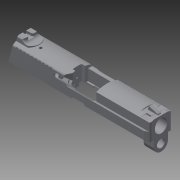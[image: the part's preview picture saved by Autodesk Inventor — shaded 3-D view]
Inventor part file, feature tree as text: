
AUTODESK INVENTOR PART (.ipt)
format: ipt  version: 2014 SP1 (Build 180222100, 222)  size: 2,646,528 bytes
history: native  units: in
note: dims shown in document units (in); Inventor stores cm internally (conversion verified against a paired STEP export)
features: sketch x85, projected_geometry x80, extrude x69, plane x11, other x6, fillet x5, mirror x5, loft x4, revolve x4, chamfer x2, emboss x2, pattern_linear x1, reference x1
ambient origin geometry x8: Origin, YZ Plane, XZ Plane, XY Plane, X Axis, Y Axis, Z Axis, Center Point
bodies: Body1 (feature_tree), Body2 (feature_tree), Body3 (feature_tree)
feature tree (275):
  other  "Slide"
  extrude  "Extrusion1"  Depth=0.868in
  sketch  "Sketch3"  dims[d5=1.0545in d6=0.0in d7=105.0deg]
  loft  "Loft1"
  extrude  "Extrusion2"  TaperAngle=105.0deg  [1 undecoded]
  extrude  "Extrusion3"  Depth=0.5in
  extrude  "Extrusion4"  Depth=0.5in
  other  "Top Plane"
  extrude  "Extrusion5"  TaperAngle=0.0deg  [1 undecoded]
  extrude  "Extrusion6"  Depth=0.6385in
  extrude  "Extrusion7"  Depth=0.3515in
  extrude  "Extrusion8"  Depth=0.595in TaperAngle=0.0deg
  extrude  "Extrusion9"  Depth=2.4555in
  plane  "Work Plane2"
  extrude  "Extrusion10"  Depth=0.595in TaperAngle=0.0deg
  extrude  "Extrusion11"  Depth=0.595in TaperAngle=0.0deg
  revolve  "Revolution1"  [1 undecoded]
  extrude  "Extrusion12"  Depth=0.507in
  extrude  "Extrusion13"  Depth=0.125in
  extrude  "Extrusion14"  Depth=0.588in
  extrude  "Extrusion15"  Depth=0.1138in
  sketch  "Sketch22"  dims[d52=0.091in d53=0.182in]
  plane  "Work Plane5"
  extrude  "Extrusion16"  Depth=0.135in
  extrude  "Extrusion17"  Depth=0.8675in
  extrude  "Extrusion18"  Depth=0.182in
  extrude  "Extrusion19"  Depth=0.553in
  extrude  "Extrusion20"  Depth=0.581in TaperAngle=0.0deg
  extrude  "Extrusion21"  Depth=0.058in
  sketch  "Sketch30"  dims[d75=0.6285in d76=0.0in d77=30.0deg]
  other  "Work Point1"
  sketch  "Sketch31"  dims[d78=0.6285in d79=0.0in d80=1.2325in]
  sketch  "Sketch33"  dims[d83=0.6285in d84=0.0in d85=0.0902in]
  sketch  "Sketch32"  dims[d81=0.36in d82=0.07in]
  loft  "Loft3"
  revolve  "Revolution2"  [1 undecoded]
  extrude  "Extrusion22"  Depth=0.588in
  extrude  "Extrusion23"  TaperAngle=30.0deg  [1 undecoded]
  extrude  "Extrusion24"  Depth=1.2325in
  sketch  "Sketch38"  dims[d98=0.236in d99=0.0555in d100=0.0in]
  extrude  "Extrusion25"  Depth=0.07in
  extrude  "Extrusion26"  Depth=0.0902in
  extrude  "Extrusion27"  Depth=1.906in
  extrude  "Extrusion28"  Depth=0.2325in TaperAngle=0.0deg
  extrude  "Extrusion29"  Depth=0.6285in TaperAngle=0.0deg
  extrude  "Extrusion30"  Depth=0.1195in
  extrude  "Extrusion31"  Depth=0.0555in TaperAngle=0.0deg
  extrude  "Extrusion32"  Depth=0.063in TaperAngle=0.0deg
  extrude  "Extrusion33"  Depth=0.05in
  plane  "Work Plane6"
  extrude  "Extrusion34"  Depth=0.2in
  extrude  "Extrusion35"  Depth=0.125in
  extrude  "Extrusion36"  TaperAngle=0.0deg  [1 undecoded]
  extrude  "Extrusion37"  TaperAngle=45.0deg  [1 undecoded]
  plane  "Work Plane7"
  extrude  "Extrusion38"  Depth=0.2in
  extrude  "Extrusion39"  Depth=0.6315in
  extrude  "Extrusion40"  Depth=0.4688in
  extrude  "Extrusion41"  Depth=0.942in
  fillet  "Fillet1"  Radius=0.126in
  plane  "Work Plane8"
  extrude  "Extrusion42"  Depth=0.205in
  extrude  "Extrusion43"  Depth=0.1585in
  pattern_linear  "Rectangular Pattern1"  Spacing1=0.1345in  [1 undecoded]
  mirror  "Mirror1"
  extrude  "Extrusion44"  Depth=0.015in
  extrude  "Extrusion55"  Depth=0.015in
  sketch  "Sketch69"  dims[d162=0.167in]
  chamfer  "Chamfer2"  Distance=0.4735in
  other  "Work Point2"
  extrude  "Extrusion56"  Depth=0.015in
  loft  "Loft5"
  extrude  "Extrusion45"  Depth=0.015in
  mirror  "Mirror2"
  extrude  "Extrusion46"  [1 undecoded]
  extrude  "Extrusion47"  Depth=0.015in
  extrude  "Extrusion48"  Depth=0.015in
  extrude  "Extrusion49"  Depth=0.015in
  sketch  "Sketch62"  dims[d152=0.133in]
  extrude  "Extrusion50"  Depth=0.015in
  extrude  "Extrusion51"  Depth=0.015in
  extrude  "Extrusion52"  Depth=0.015in TaperAngle=0.0deg
  extrude  "Extrusion53"  Depth=0.015in
  fillet  "Fillet2"  Radius=0.118in
  fillet  "Fillet3"  Radius=0.016in
  chamfer  "Chamfer1"  Distance=3.937in
  sketch  "Sketch67"  dims[d159=0.13in]
  emboss  "Emboss1"
  emboss  "Emboss2"
  extrude  "Extrusion54"  TaperAngle=60.0deg  [1 undecoded]
  extrude  "Extrusion57"  Depth=0.015in
  mirror  "Mirror3"
  fillet  "Fillet4"  Radius=0.059in
  extrude  "Extrusion58"  Depth=0.015in
  extrude  "Extrusion59"  Depth=0.015in TaperAngle=0.0deg
  revolve  "Revolution3"  [1 undecoded]
  extrude  "Extrusion60"  Depth=0.015in
  extrude  "Extrusion61"  Depth=0.015in TaperAngle=0.0deg
  plane  "Work Plane9"
  extrude  "Extrusion62"  Depth=0.015in
  sketch  "Sketch81"  dims[d177=0.12in]
  plane  "Work Plane10"
  sketch  "Sketch83"  dims[d178=0.289in]
  loft  "Loft6"
  extrude  "Extrusion64"  Depth=0.015in TaperAngle=0.0deg
  extrude  "Extrusion65"  Depth=0.015in
  extrude  "Extrusion66"  Depth=0.015in TaperAngle=0.0deg
  extrude  "Extrusion67"  Depth=0.015in
  extrude  "Extrusion68"  Depth=0.015in TaperAngle=0.0deg
  extrude  "Extrusion69"  Depth=0.015in TaperAngle=0.0deg
  plane  "Work Plane11"
  revolve  "Revolution4"  [1 undecoded]
  mirror  "Mirror4"
  extrude  "Extrusion70"  Depth=0.015in TaperAngle=0.0deg
  fillet  "Fillet5"  Radius=0.374in
  mirror  "Mirror5"
  plane  "Work Plane12"
  sketch  "Sketch1"  dims[d0=6.506in d1=0.868in]
  sketch  "Sketch2"  dims[d2=1.0545in d3=0.0in d4=1.25in]
  projected_geometry  "Projected Loop1"
  sketch  "Sketch4"  dims[d8=1.625in d9=0.5in]
  projected_geometry  "Projected Loop2"
  sketch  "Sketch5"  dims[d10=1.625in d11=0.5in]
  projected_geometry  "Projected Loop3"
  sketch  "Sketch6"  dims[d12=0.0in d13=90.0deg d14=0.0in d15=90.0deg]
  projected_geometry  "Projected Loop4"
  sketch  "Sketch7"  dims[d16=0.471in d17=0.6385in]
  projected_geometry  "Projected Loop5"
  sketch  "Sketch8"  dims[d18=0.595in d19=0.0in d20=0.3515in]
  projected_geometry  "Projected Loop6"
  sketch  "Sketch9"  dims[d21=0.1435in d22=0.595in d23=0.0in]
  sketch  "Sketch10"  dims[d24=0.666in d25=2.4555in]
  projected_geometry  "Projected Loop7"
  sketch  "Sketch11"  dims[d26=1.2025in d27=0.595in d28=0.0in]
  projected_geometry  "Projected Loop8"
  sketch  "Sketch12"  dims[d29=0.69in d30=0.595in d31=0.0in]
  projected_geometry  "Projected Loop9"
  sketch  "Sketch13"  dims[d32=0.154in d33=0.41in]
  projected_geometry  "Projected Loop10"
  sketch  "Sketch14"  dims[d34=0.595in d35=0.0in d36=0.507in]
  projected_geometry  "Projected Loop11"
  sketch  "Sketch17"  dims[d37=0.787in d40=0.125in]
  sketch  "Sketch18"  dims[d41=0.588in d42=0.588in]
  projected_geometry  "Projected Loop13"
  sketch  "Sketch19"  dims[d43=0.724in d44=0.0in d45=0.1138in]
  projected_geometry  "Projected Loop14"
  sketch  "Sketch20"  dims[d47=0.135in d48=0.135in]
  sketch  "Sketch21"  dims[d49=0.2685in d50=0.0in d51=0.8675in]
  plane  "Work Plane3"
  plane  "Work Plane4"
  sketch  "Sketch24"  dims[d54=0.2685in d55=0.0in d56=0.553in]
  sketch  "Sketch25"  dims[d57=0.223in d58=0.581in d59=0.0in]
  projected_geometry  "Projected Loop15"
  sketch  "Sketch26"  dims[d66=0.268in d67=0.058in]
  projected_geometry  "Projected Loop16"
  projected_geometry  "Projected Loop17"
  sketch  "Sketch27"  dims[d68=90.0deg d69=0.057in]
  projected_geometry  "Projected Loop18"
  sketch  "Sketch28"  dims[d70=0.057in d71=0.0625in]
  projected_geometry  "Projected Loop19"
  sketch  "Sketch29"  dims[d72=0.031in d73=0.0in d74=0.588in]
  projected_geometry  "Projected Loop20"
  projected_geometry  "Projected Loop21"
  sketch  "Sketch34"  dims[d86=0.4435in d87=1.906in]
  projected_geometry  "Projected Loop22"
  sketch  "Sketch35"  dims[d88=0.2405in d89=0.0in d90=0.2325in]
  projected_geometry  "Projected Loop23"
  sketch  "Sketch36"  dims[d92=0.18in d93=0.6285in d94=0.0in]
  sketch  "Sketch37"  dims[d95=0.6285in d96=0.0in d97=0.1195in]
  projected_geometry  "Projected Loop24"
  sketch  "Sketch39"  dims[d101=0.0555in d102=0.0in d103=0.063in d104=0.0in]
  projected_geometry  "Projected Loop25"
  sketch  "Sketch40"  dims[d105=0.126in d106=0.0in d107=0.05in]
  projected_geometry  "Projected Loop26"
  sketch  "Sketch41"  dims[d108=0.125in d109=0.2in]
  projected_geometry  "Projected Loop27"
  sketch  "Sketch42"  dims[d110=45.0deg d111=0.125in]
  sketch  "Sketch43"  dims[d112=0.0in d113=90.0deg d114=0.0in d115=90.0deg]
  projected_geometry  "Projected Loop28"
  sketch  "Sketch44"  dims[d116=0.125in d117=45.0deg]
  sketch  "Sketch45"  dims[d118=0.404in d119=0.2in]
  projected_geometry  "Projected Loop29"
  projected_geometry  "Projected Loop30"
  projected_geometry  "Projected Loop31"
  projected_geometry  "Projected Loop32"
  sketch  "Sketch46"  dims[d120=1.9in d121=0.6315in]
  sketch  "Sketch47"  dims[d122=0.126in d123=0.0in d124=0.4688in]
  projected_geometry  "Projected Loop33"
  sketch  "Sketch48"  dims[d125=0.077in d126=0.942in d127=0.126in d128=0.0in]
  sketch  "Sketch49"  dims[d129=0.1035in d130=0.205in]
  projected_geometry  "Projected Loop34"
  sketch  "Sketch50"  dims[d131=0.126in d132=0.0in d133=0.1585in]
  projected_geometry  "Projected Loop35"
  sketch  "Sketch51"  dims[d134=0.209in d135=0.0in]
  projected_geometry  "Projected Loop36"
  projected_geometry  "Projected Loop37"
  sketch  "Sketch52"  dims[d136=0.159in d137=0.0in]
  projected_geometry  "Projected Loop38"
  sketch  "Sketch53"  dims[d138=0.159in d139=0.0in]
  projected_geometry  "Projected Loop39"
  sketch  "Sketch54"  dims[d140=0.118in]
  sketch  "Sketch55"  dims[d141=0.485in]
  projected_geometry  "Projected Loop40"
  sketch  "Sketch56"  dims[d143=0.159in d144=0.0in]
  sketch  "Sketch57"  dims[d145=0.0156in]
  projected_geometry  "Projected Loop41"
  projected_geometry  "Projected Loop42"
  sketch  "Sketch58"  dims[d146=0.0745in]
  projected_geometry  "Projected Loop43"
  sketch  "Sketch59"  dims[d148=0.439in]
  sketch  "Sketch60"  dims[d149=2.95in]
  projected_geometry  "Projected Loop44"
  sketch  "Sketch61"  dims[d150=0.159in d151=0.0in]
  projected_geometry  "Projected Loop45"
  sketch  "Sketch63"  dims[d153=0.159in d154=0.0in]
  projected_geometry  "Projected Loop46"
  sketch  "Sketch64"  dims[d155=3.422in]
  projected_geometry  "Projected Loop47"
  projected_geometry  "Projected Loop48"
  sketch  "Sketch65"  dims[d156=0.46in]
  projected_geometry  "Projected Loop49"
  sketch  "Sketch66"  dims[d157=0.159in d158=0.0in]
  projected_geometry  "Projected Loop50"
  projected_geometry  "Projected Loop51"
  sketch  "Sketch68"  dims[d160=0.159in d161=0.0in]
  projected_geometry  "Projected Loop52"
  projected_geometry  "Projected Loop53"
  sketch  "Sketch71"  dims[d163=0.159in d164=0.0in]
  sketch  "Sketch73"  dims[d165=-0.55in]
  projected_geometry  "Projected Loop54"
  sketch  "Sketch74"  dims[d168=0.3465in d169=0.0in]
  other  "Front Sight"
  sketch  "Sketch75"  dims[d170=0.07in]
  sketch  "Sketch76"  dims[d171=0.42in]
  sketch  "Sketch78"  dims[d172=0.3465in d173=0.0in]
  sketch  "Sketch79"  dims[d174=0.2385in]
  projected_geometry  "Projected Loop56"
  sketch  "Sketch80"  dims[d175=1.7405in d176=0.0in]
  reference  "Reference1"
  projected_geometry  "Projected Loop57"
  projected_geometry  "Projected Loop58"
  sketch  "Sketch84"  dims[d179=0.5715in]
  other  "Rear Sight"
  sketch  "Sketch85"  dims[d180=1.7405in d181=0.0in]
  sketch  "Sketch86"  dims[d182=0.196in]
  projected_geometry  "Projected Loop60"
  sketch  "Sketch87"  dims[d183=2.303in d184=0.0in]
  projected_geometry  "Projected Loop61"
  projected_geometry  "Projected Loop62"
  sketch  "Sketch88"  dims[d185=0.12in]
  projected_geometry  "Projected Loop63"
  sketch  "Sketch89"  dims[d186=1.374in]
  projected_geometry  "Projected Loop64"
  sketch  "Sketch90"  dims[d187=0.09in]
  projected_geometry  "Projected Loop65"
  projected_geometry  "Projected Loop66"
  sketch  "Sketch91"  dims[d188=0.142in d189=0.0in]
  sketch  "Sketch92"  dims[d191=0.2525in d192=0.1345in d193=0.22in d194=0.1215in d195=0.4735in d196=0.0in d197=1.431in d198=0.763in d199=0.0in d200=0.125in d201=-0.36in d202=1.5in d203=0.041in d204=1.5in d205=0.041in d206=3.457in d207=0.763in d208=0.0in d209=0.132in d210=0.118in d211=0.016in d212=0.0in d213=3.937in d215=0.171in d216=60.0deg d217=0.3in d218=0.059in d219=0.19in d220=1.891in d221=0.0in d222=0.0625in d223=0.0825in d224=1.891in d225=0.0in d226=0.184in d228=0.067in d229=0.2785in d230=0.0in d231=0.4965in d232=0.374in d233=0.0in d235=0.3in d236=0.374in d237=0.0in d239=0.374in d240=0.0in d241=0.6835in d242=0.374in d243=0.0in d244=0.374in d245=0.0in d246=0.6765in d247=0.547in d248=0.374in d249=0.0in d251=0.027in d252=0.0in d253=0.027in d254=0.0156in d255=0.01in d256=0.125in d257=45.0deg d258=0.002in d259=0.0in d260=0.002in d261=0.0in d262=0.002in d263=0.0in d264=45.0deg d265=0.027in d266=0.0in d267=45.0deg d268=0.041in d269=0.125in d270=45.0deg d277=0.054in d278=0.0in d279=0.0in d280=90.0deg d281=0.0in d282=90.0deg d283=0.0938in d284=0.054in d285=0.0in d286=0.0078in d287=0.466in d288=0.002in d289=0.7559in d290=0.1635in d291=0.05in d292=0.5355in d293=0.1365in d294=0.0in d295=0.468in d296=0.0in d297=90.0deg d298=0.468in d299=0.0in d300=0.468in d301=0.0in d302=0.551in d303=1.0in d304=0.0in d305=0.667in d306=0.6925in d307=0.4062in d308=0.2in d309=0.125in d313=0.2965in d314=0.0in d315=90.0deg d316=0.0in d317=90.0deg d318=0.14in d320=0.14in d321=0.0in d322=0.287in d324=0.272in d325=0.3969in d326=0.125in d327=0.2075in d328=0.0in d329=0.1925in d330=0.0038in d331=0.0038in d332=0.0038in d333=0.2075in d334=0.0in d335=0.3885in d336=0.097in d337=0.0in d338=60.0deg d339=0.18in d340=0.151in d341=0.06in d342=0.07in d343=0.111in d344=0.0in d345=45.0deg d346=45.0deg d347=0.066in d348=0.111in d349=0.0in d350=-0.125in d351=90.0deg d352=0.1185in d353=0.0995in d354=0.0225in d355=0.0in d356=0.015in]
  projected_geometry  "Projected Loop67"
  projected_geometry  "Project Cut Edges1"
  projected_geometry  "Project Cut Edges2"
  projected_geometry  "Project Cut Edges4"
  projected_geometry  "Project Cut Edges5"
  projected_geometry  "Project Cut Edges6"
  projected_geometry  "Project Cut Edges7"
  projected_geometry  "Project Cut Edges8"
  projected_geometry  "Project Cut Edges9"
  projected_geometry  "Project Cut Edges10"
  projected_geometry  "Project Cut Edges11"
  projected_geometry  "Project Cut Edges12"
  projected_geometry  "Project Cut Edges13"
  projected_geometry  "Project Cut Edges14"
  projected_geometry  "Project Cut Edges16"
  projected_geometry  "Project Cut Edges17"
  projected_geometry  "Project Cut Edges18"
note: 12 required parameter values undecoded (feature->parameter linkage not recoverable at this tier; creation-order binding heuristic only, values carry confidence <= 0.55)